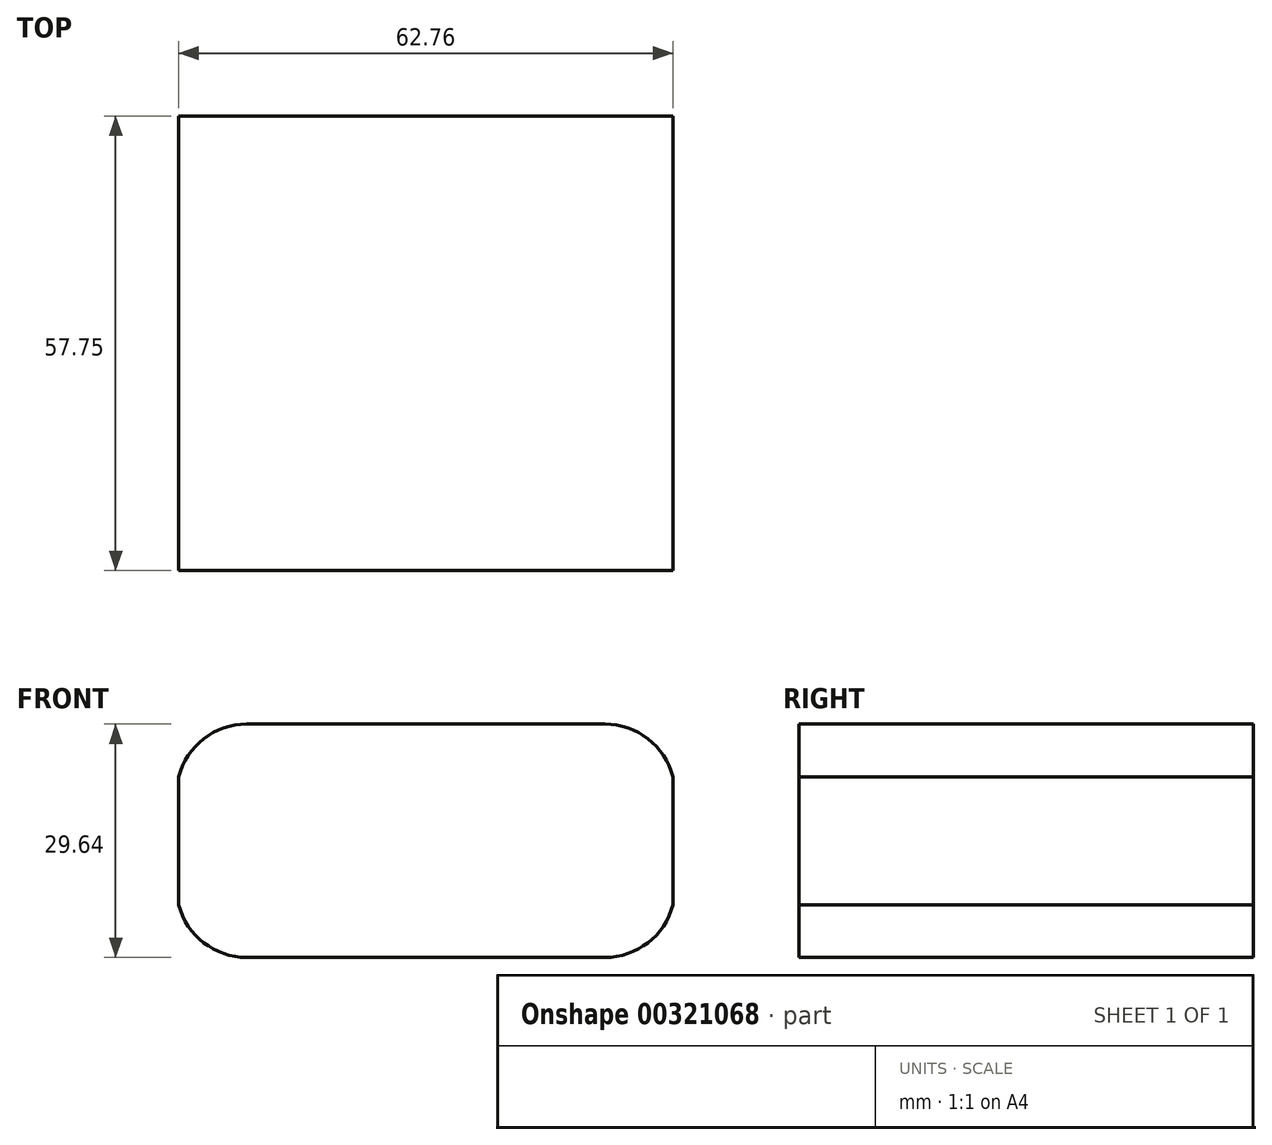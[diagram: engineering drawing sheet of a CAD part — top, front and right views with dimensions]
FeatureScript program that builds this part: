
annotation { "Feature Type Name" : "Feature", "Feature Type Description" : "" }
export const myFeature = defineFeature(function(context is Context, id is Id, definition is map)
    precondition{}
    {
        {
            var Q0;
            Q0=qCreatedBy(makeId("Front.planeOp"),FACE);
            var sketch = newSketch(context, id + "F0", { "sketchPlane" : qUnion([Q0])});
            skLineSegment(sketch, "E0.bottom", {"start": v(31.38, 14.83) * mm, "end": v(-31.38, 14.83) * mm, "construction": true});
            skLineSegment(sketch, "E0.top", {"start": v(31.38, -14.82) * mm, "end": v(-31.38, -14.82) * mm, "construction": true});
            skLineSegment(sketch, "E0.left", {"start": v(31.38, 14.83) * mm, "end": v(31.38, -14.82) * mm, "construction": true});
            skLineSegment(sketch, "E0.right", {"start": v(-31.38, 14.82) * mm, "end": v(-31.38, -14.82) * mm, "construction": true});
            skPoint(sketch, "E0.middle", {"position": v(0, 0) * mm});
            skLineSegment(sketch, "E1.bottom", {"start": v(22.75, 14.83) * mm, "end": v(-22.75, 14.83) * mm, "construction": true});
            skLineSegment(sketch, "E1.top", {"start": v(22.75, -14.83) * mm, "end": v(-22.75, -14.83) * mm, "construction": true});
            skLineSegment(sketch, "E1.left", {"start": v(22.75, 14.82) * mm, "end": v(22.75, -14.82) * mm, "construction": true});
            skLineSegment(sketch, "E1.right", {"start": v(-22.75, 14.82) * mm, "end": v(-22.75, -14.82) * mm, "construction": true});
            skLineSegment(sketch, "E2.bottom", {"start": v(-31.38, 8.14) * mm, "end": v(31.38, 8.14) * mm, "construction": true});
            skLineSegment(sketch, "E2.top", {"start": v(-31.38, -8.14) * mm, "end": v(31.38, -8.14) * mm, "construction": true});
            skLineSegment(sketch, "E2.left", {"start": v(-31.38, 8.14) * mm, "end": v(-31.38, -8.14) * mm, "construction": true});
            skLineSegment(sketch, "E2.right", {"start": v(31.38, 8.14) * mm, "end": v(31.38, -8.14) * mm, "construction": true});
            skArc(sketch, "E3", {"start": v(-22.75, 14.83) * mm, "mid": v(-28.2, 12.96) * mm, "end": v(-31.38, 8.14) * mm});
            skArc(sketch, "E4", {"start": v(-31.38, -8.14) * mm, "mid": v(-28.2, -12.96) * mm, "end": v(-22.75, -14.83) * mm});
            skArc(sketch, "E5", {"start": v(31.38, 8.14) * mm, "mid": v(28.2, 12.96) * mm, "end": v(22.75, 14.83) * mm});
            skArc(sketch, "E6", {"start": v(22.75, -14.83) * mm, "mid": v(28.2, -12.96) * mm, "end": v(31.38, -8.14) * mm});
            skLineSegment(sketch, "E7", {"start": v(-22.75, 14.83) * mm, "end": v(22.75, 14.83) * mm});
            skLineSegment(sketch, "E8", {"start": v(31.38, 8.14) * mm, "end": v(31.38, -8.14) * mm});
            skLineSegment(sketch, "E9", {"start": v(22.75, -14.83) * mm, "end": v(-22.75, -14.83) * mm});
            skLineSegment(sketch, "E10", {"start": v(-31.38, -8.14) * mm, "end": v(-31.38, 8.14) * mm});
            skSolve(sketch);
        }
        {
            var Q0;
            Q0 = qSketchRegion(id + "F0", true);
            extrude(context, id + "F1", {"entities" : qUnion([Q0]), "depth" : 57.75 * mm});
        }
    });
